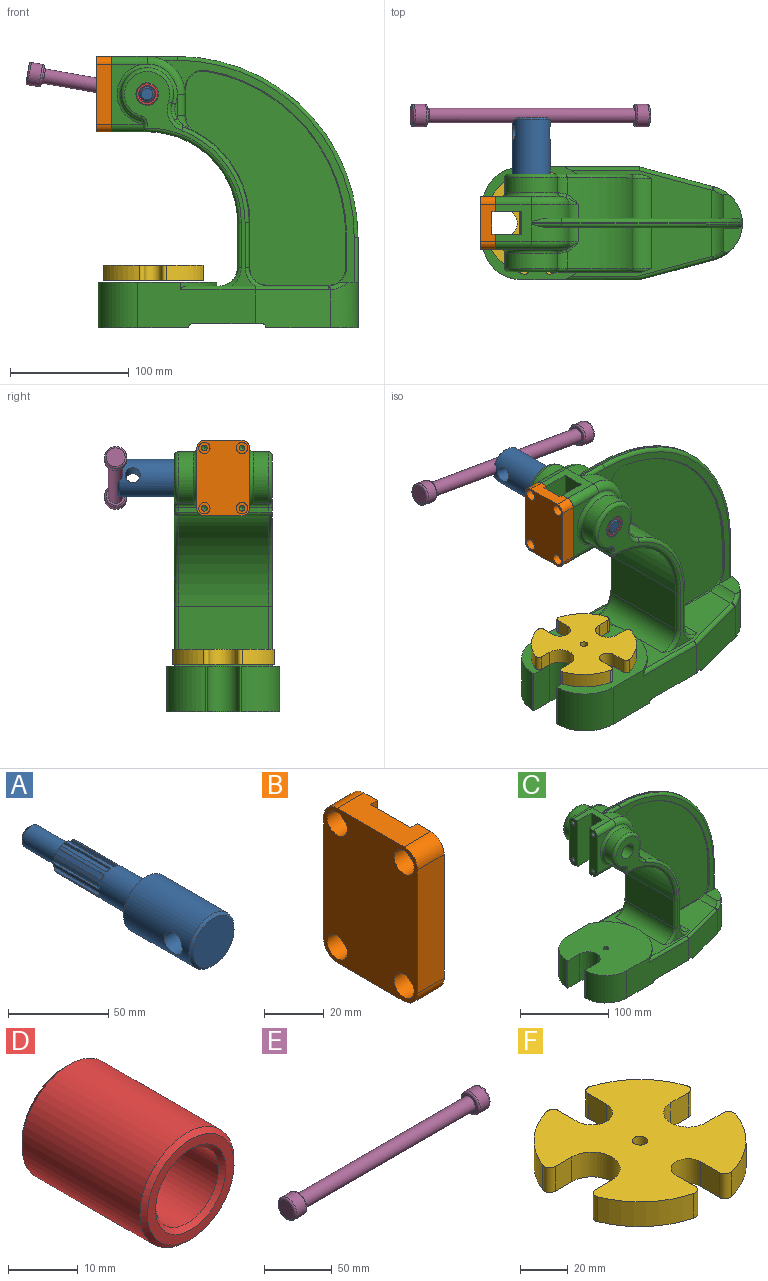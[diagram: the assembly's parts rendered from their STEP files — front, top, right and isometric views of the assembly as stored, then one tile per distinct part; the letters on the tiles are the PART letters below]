
ASSEMBLY  parts=6 mates=4
PART A: 94 faces, bbox 31.8x130.2x31.8 mm
  f0: cone r=8mm half-angle=45deg, axis (0,-1,0), area 3.4mm2, adj f11,f18,f83,f87
  f1: cone r=8mm half-angle=45deg, axis (0,-1,0), area 3.4mm2, adj f11,f18,f77,f81
  f2: cone r=8mm half-angle=45deg, axis (0,-1,0), area 3.4mm2, adj f11,f18,f71,f75
  f3: cone r=8mm half-angle=45deg, axis (0,-1,0), area 3.4mm2, adj f11,f18,f65,f69
  f4: cone r=8mm half-angle=45deg, axis (0,-1,0), area 3.4mm2, adj f11,f18,f59,f63
  f5: cone r=8mm half-angle=45deg, axis (0,-1,0), area 3.4mm2, adj f11,f18,f53,f57
  f6: cone r=8mm half-angle=45deg, axis (0,-1,0), area 3.4mm2, adj f11,f18,f47,f51
  f7: cone r=8mm half-angle=45deg, axis (0,-1,0), area 3.4mm2, adj f11,f18,f41,f45
  f8: cone r=8mm half-angle=45deg, axis (0,-1,0), area 3.4mm2, adj f11,f18,f35,f39
  f9: cone r=8mm half-angle=45deg, axis (0,-1,0), area 3.4mm2, adj f11,f18,f29,f33
  f10: cone r=8mm half-angle=45deg, axis (0,-1,0), area 3.4mm2, adj f11,f18,f23,f27
  f11: cylinder r=9.53mm len=55.63mm, axis (0,-1,0), area 2118.8mm2, adj f0,f1,f2,f3,f4,f5,f6,f7
  f12: plane 31.75x31.75mm, normal (0,1,0), area 506.7mm2, adj f11,f13
  f13: cylinder r=15.88mm len=46.1mm, axis (0,-1,0), area 4339.6mm2, adj f12,f15,f16
  f14: plane 28.7x28.7mm, normal (0,-1,0), area 647mm2, adj f15
  f15: cone r=14.35mm half-angle=45deg, axis (0,1,0), area 204.7mm2, adj f13,f14
  f16: cylinder r=6.35mm len=31.75mm, axis (1,0,0), area 1214.5mm2, adj f13
  f17: cylinder r=6.35mm len=23.88mm, axis (0,1,0), area 952.6mm2, adj f18,f93
  f18: plane 16x16mm, normal (0,1,0), area 67.3mm2, adj f0,f1,f2,f3,f4,f5,f6,f7
  f19: plane 9.65x9.65mm, normal (0,1,0), area 73.2mm2, adj f93
  f20: cone r=8mm half-angle=45deg, axis (0,-1,0), area 3.4mm2, adj f11,f18,f21,f89
  f21: plane 31.76x1.55mm, normal (0.36,0,-0.93), area 51.4mm2, adj f11,f18,f20,f22,f24
  f22: plane 31.75x2.7mm, normal (0.97,0,0.26), area 88.7mm2, adj f18,f21,f23,f25
  f23: plane 31.76x1.65mm, normal (-0.15,0,0.99), area 51.4mm2, adj f10,f11,f18,f22,f26
  f24: cone r=1.78mm half-angle=83.9deg, axis (0.26,0,-0.97), area 1.5mm2, adj f11,f21,f25
  f25: cylinder r=1.78mm len=3.16mm, axis (0.26,0,-0.97), area 7.7mm2, adj f11,f22,f24,f26
  f26: cone r=0mm half-angle=83.9deg, axis (-0.26,0,0.97), area 1.5mm2, adj f11,f23,f25
  f27: plane 31.76x1.65mm, normal (-0.15,0,-0.99), area 51.4mm2, adj f10,f11,f18,f28,f30
  f28: plane 31.75x2.7mm, normal (0.97,0,-0.26), area 88.7mm2, adj f18,f27,f29,f31
  f29: plane 31.76x1.55mm, normal (0.36,0,0.93), area 51.4mm2, adj f9,f11,f18,f28,f32
  f30: cone r=1.78mm half-angle=83.9deg, axis (-0.26,0,-0.97), area 1.5mm2, adj f11,f27,f31
  f31: cylinder r=1.78mm len=3.16mm, axis (-0.26,0,-0.97), area 7.7mm2, adj f11,f28,f30,f32
  f32: cone r=0mm half-angle=83.9deg, axis (0.26,0,0.97), area 1.5mm2, adj f11,f29,f31
  f33: plane 31.76x1.3mm, normal (-0.63,0,-0.78), area 51.4mm2, adj f9,f11,f18,f34,f36
  f34: plane 31.75x1.98mm, normal (0.71,0,-0.71), area 88.7mm2, adj f18,f33,f35,f37
  f35: plane 31.76x1.3mm, normal (0.78,0,0.63), area 51.4mm2, adj f8,f11,f18,f34,f38
  f36: cone r=1.78mm half-angle=83.9deg, axis (-0.71,0,-0.71), area 1.5mm2, adj f11,f33,f37
  f37: cylinder r=1.78mm len=3.16mm, axis (-0.71,0,-0.71), area 7.5mm2, adj f11,f34,f36,f38
  f38: cone r=0mm half-angle=83.9deg, axis (0.71,0,0.71), area 1.5mm2, adj f11,f35,f37
  f39: plane 31.76x1.55mm, normal (-0.93,0,-0.36), area 51.4mm2, adj f8,f11,f18,f40,f42
  f40: plane 31.75x2.7mm, normal (0.26,0,-0.97), area 88.7mm2, adj f18,f39,f41,f43
  f41: plane 31.76x1.65mm, normal (0.99,0,0.15), area 51.4mm2, adj f7,f11,f18,f40,f44
  f42: cone r=1.78mm half-angle=83.9deg, axis (-0.97,0,-0.26), area 1.5mm2, adj f11,f39,f43
  f43: cylinder r=1.78mm len=3.16mm, axis (-0.97,0,-0.26), area 7.7mm2, adj f11,f40,f42,f44
  f44: cone r=0mm half-angle=83.9deg, axis (0.97,0,0.26), area 1.5mm2, adj f11,f41,f43
  f45: plane 31.76x1.65mm, normal (-0.99,0,0.15), area 51.4mm2, adj f7,f11,f18,f46,f48
  f46: plane 31.75x2.7mm, normal (-0.26,0,-0.97), area 88.7mm2, adj f18,f45,f47,f49
  f47: plane 31.76x1.55mm, normal (0.93,0,-0.36), area 51.4mm2, adj f6,f11,f18,f46,f50
  f48: cone r=1.78mm half-angle=83.9deg, axis (-0.97,0,0.26), area 1.5mm2, adj f11,f45,f49
  f49: cylinder r=1.78mm len=3.16mm, axis (-0.97,0,0.26), area 7.7mm2, adj f11,f46,f48,f50
  f50: cone r=0mm half-angle=83.9deg, axis (0.97,0,-0.26), area 1.5mm2, adj f11,f47,f49
  f51: plane 31.76x1.3mm, normal (-0.78,0,0.63), area 51.4mm2, adj f6,f11,f18,f52,f54
  f52: plane 31.75x1.98mm, normal (-0.71,0,-0.71), area 88.7mm2, adj f18,f51,f53,f55
  f53: plane 31.76x1.3mm, normal (0.63,0,-0.78), area 51.4mm2, adj f5,f11,f18,f52,f56
  f54: cone r=1.78mm half-angle=83.9deg, axis (-0.71,0,0.71), area 1.5mm2, adj f11,f51,f55
  f55: cylinder r=1.78mm len=3.16mm, axis (-0.71,0,0.71), area 7.5mm2, adj f11,f52,f54,f56
  f56: cone r=0mm half-angle=83.9deg, axis (0.71,0,-0.71), area 1.5mm2, adj f11,f53,f55
  f57: plane 31.76x1.55mm, normal (-0.36,0,0.93), area 51.4mm2, adj f5,f11,f18,f58,f60
  f58: plane 31.75x2.7mm, normal (-0.97,0,-0.26), area 88.7mm2, adj f18,f57,f59,f61
  f59: plane 31.76x1.65mm, normal (0.15,0,-0.99), area 51.4mm2, adj f4,f11,f18,f58,f62
  f60: cone r=1.78mm half-angle=83.9deg, axis (-0.26,0,0.97), area 1.5mm2, adj f11,f57,f61
  f61: cylinder r=1.78mm len=3.16mm, axis (-0.26,0,0.97), area 7.7mm2, adj f11,f58,f60,f62
  f62: cone r=0mm half-angle=83.9deg, axis (0.26,0,-0.97), area 1.5mm2, adj f11,f59,f61
  f63: plane 31.76x1.65mm, normal (0.15,0,0.99), area 51.4mm2, adj f4,f11,f18,f64,f66
  f64: plane 31.75x2.7mm, normal (-0.97,0,0.26), area 88.7mm2, adj f18,f63,f65,f67
  f65: plane 31.76x1.55mm, normal (-0.36,0,-0.93), area 51.4mm2, adj f3,f11,f18,f64,f68
  f66: cone r=1.78mm half-angle=83.9deg, axis (0.26,0,0.97), area 1.5mm2, adj f11,f63,f67
  f67: cylinder r=1.78mm len=3.16mm, axis (0.26,0,0.97), area 7.7mm2, adj f11,f64,f66,f68
  f68: cone r=0mm half-angle=83.9deg, axis (-0.26,0,-0.97), area 1.5mm2, adj f11,f65,f67
  f69: plane 31.76x1.3mm, normal (0.63,0,0.78), area 51.4mm2, adj f3,f11,f18,f70,f72
  f70: plane 31.75x1.98mm, normal (-0.71,0,0.71), area 88.7mm2, adj f18,f69,f71,f73
  f71: plane 31.76x1.3mm, normal (-0.78,0,-0.63), area 51.4mm2, adj f2,f11,f18,f70,f74
  f72: cone r=1.78mm half-angle=83.9deg, axis (0.71,0,0.71), area 1.5mm2, adj f11,f69,f73
  f73: cylinder r=1.78mm len=3.16mm, axis (0.71,0,0.71), area 7.5mm2, adj f11,f70,f72,f74
  f74: cone r=0mm half-angle=83.9deg, axis (-0.71,0,-0.71), area 1.5mm2, adj f11,f71,f73
  f75: plane 31.76x1.55mm, normal (0.93,0,0.36), area 51.4mm2, adj f2,f11,f18,f76,f78
  f76: plane 31.75x2.7mm, normal (-0.26,0,0.97), area 88.7mm2, adj f18,f75,f77,f79
  f77: plane 31.76x1.65mm, normal (-0.99,0,-0.15), area 51.4mm2, adj f1,f11,f18,f76,f80
  f78: cone r=1.78mm half-angle=83.9deg, axis (0.97,0,0.26), area 1.5mm2, adj f11,f75,f79
  f79: cylinder r=1.78mm len=3.16mm, axis (0.97,0,0.26), area 7.7mm2, adj f11,f76,f78,f80
  f80: cone r=0mm half-angle=83.9deg, axis (-0.97,0,-0.26), area 1.5mm2, adj f11,f77,f79
  f81: plane 31.76x1.65mm, normal (0.99,0,-0.15), area 51.4mm2, adj f1,f11,f18,f82,f84
  f82: plane 31.75x2.7mm, normal (0.26,0,0.97), area 88.7mm2, adj f18,f81,f83,f85
  f83: plane 31.76x1.55mm, normal (-0.93,0,0.36), area 51.4mm2, adj f0,f11,f18,f82,f86
  f84: cone r=1.78mm half-angle=83.9deg, axis (0.97,0,-0.26), area 1.5mm2, adj f11,f81,f85
  f85: cylinder r=1.78mm len=3.16mm, axis (0.97,0,-0.26), area 7.7mm2, adj f11,f82,f84,f86
  f86: cone r=0mm half-angle=83.9deg, axis (-0.97,0,0.26), area 1.5mm2, adj f11,f83,f85
  f87: plane 31.76x1.3mm, normal (0.78,0,-0.63), area 51.4mm2, adj f0,f11,f18,f88,f90
  f88: plane 31.75x1.98mm, normal (0.71,0,0.71), area 88.7mm2, adj f18,f87,f89,f91
  f89: plane 31.76x1.3mm, normal (-0.63,0,0.78), area 51.4mm2, adj f11,f18,f20,f88,f92
  f90: cone r=1.78mm half-angle=83.9deg, axis (0.71,0,-0.71), area 1.5mm2, adj f11,f87,f91
  f91: cylinder r=1.78mm len=3.16mm, axis (0.71,0,-0.71), area 7.5mm2, adj f11,f88,f90,f92
  f92: cone r=0mm half-angle=83.9deg, axis (-0.71,0,0.71), area 1.5mm2, adj f11,f89,f91
  f93: cone r=4.83mm half-angle=45deg, axis (0,-1,0), area 75.7mm2, adj f17,f19
PART B: 26 faces, bbox 12.7x44.5x63.5 mm
  f0: plane 63.5x12.7mm, normal (1,0,0), area 753.5mm2, adj f1,f2,f6,f7,f8,f14,f17,f25
  f1: cylinder r=6.35mm len=12.7mm, axis (1,0,0), area 126.7mm2, adj f0,f2,f8,f9
  f2: plane 31.75x12.7mm, normal (0,0,1), area 341.8mm2, adj f0,f1,f3,f9,f10,f23,f24,f25
  f3: cylinder r=6.35mm len=12.7mm, axis (1,0,0), area 126.7mm2, adj f2,f4,f9,f10
  f4: plane 50.8x12.7mm, normal (0,1,0), area 645.2mm2, adj f3,f5,f9,f10
  f5: cylinder r=6.35mm len=12.7mm, axis (1,0,0), area 126.7mm2, adj f4,f6,f9,f10
  f6: plane 31.75x12.7mm, normal (0,0,-1), area 341.8mm2, adj f0,f5,f7,f9,f10,f23,f24,f25
  f7: cylinder r=6.35mm len=12.7mm, axis (1,0,0), area 126.7mm2, adj f0,f6,f8,f9
  f8: plane 50.8x12.7mm, normal (0,-1,0), area 645.2mm2, adj f0,f1,f7,f9
  f9: plane 63.5x44.45mm, normal (-1,0,0), area 2502.9mm2, adj f1,f2,f3,f4,f5,f6,f7,f8
  f10: plane 63.5x12.7mm, normal (1,0,0), area 753.5mm2, adj f2,f3,f4,f5,f6,f11,f20,f24
  f11: cylinder r=2.38mm len=6.35mm, axis (-1,0,0), area 95mm2, adj f10,f12
  f12: plane 9.53x9.53mm, normal (-1,0,0), area 53.4mm2, adj f11,f13
  f13: cylinder r=4.76mm len=9.53mm, axis (-1,0,0), area 190mm2, adj f9,f12
  f14: cylinder r=2.38mm len=6.35mm, axis (-1,0,0), area 95mm2, adj f0,f15
  f15: plane 9.53x9.53mm, normal (-1,0,0), area 53.4mm2, adj f14,f16
  f16: cylinder r=4.76mm len=9.53mm, axis (-1,0,0), area 190mm2, adj f9,f15
  f17: cylinder r=2.38mm len=6.35mm, axis (-1,0,0), area 95mm2, adj f0,f18
  f18: plane 9.53x9.53mm, normal (-1,0,0), area 53.4mm2, adj f17,f19
  f19: cylinder r=4.76mm len=9.53mm, axis (-1,0,0), area 190mm2, adj f9,f18
  f20: cylinder r=2.38mm len=6.35mm, axis (-1,0,0), area 95mm2, adj f10,f21
  f21: plane 9.53x9.53mm, normal (-1,0,0), area 53.4mm2, adj f20,f22
  f22: cylinder r=4.76mm len=9.53mm, axis (-1,0,0), area 190mm2, adj f9,f21
  f23: plane 63.5x19.05mm, normal (1,0,0), area 1209.7mm2, adj f2,f6,f24,f25
  f24: plane 63.5x3.23mm, normal (0,-1,0), area 204.8mm2, adj f2,f6,f10,f23
  f25: plane 63.5x3.23mm, normal (0,1,0), area 204.8mm2, adj f0,f2,f6,f23
PART C: 180 faces, bbox 234.5x98.1x244 mm
  f0: plane 63.5x12.7mm, normal (-1,0,0), area 753.5mm2, adj f2,f15,f17,f92,f97,f149,f151,f158
  f1: plane 20.23x2.34mm, normal (0,1,0), area 23.9mm2, adj f90,f91,f104,f106
  f2: plane 50.8x30.1mm, normal (0,-1,0), area 515.4mm2, adj f0,f83,f92,f97,f124
  f3: plane 22.59x12.73mm, normal (1,0,0), area 235.4mm2, adj f19,f26,f32,f87,f94,f174
  f4: plane 22.59x12.73mm, normal (1,0,0), area 235.4mm2, adj f10,f14,f33,f86,f90,f164
  f5: plane 99.19x38.1mm, normal (0,-1,0), area 3202mm2, adj f6,f40,f46,f49,f52,f58,f76,f133
  f6: plane 100x95.25mm, normal (0,0,1), area 7398mm2, adj f5,f43,f44,f48,f54,f55,f56,f57
  f7: plane 38.1x34.96mm, normal (1,0,0), area 1331.9mm2, adj f8,f9,f114,f169
  f8: cylinder r=15.88mm len=34.96mm, axis (0,1,0), area 871.7mm2, adj f7,f37,f115,f167
  f9: cylinder r=85.72mm len=80.21mm, axis (0,1,0), area 3442.3mm2, adj f7,f80,f86,f100,f113,f168
  f10: cylinder r=15.88mm len=18.65mm, axis (0,1,0), area 22.7mm2, adj f4,f11,f33,f162
  f11: cylinder r=142.88mm len=140.67mm, axis (0,1,0), area 163.3mm2, adj f10,f12,f33,f160
  f12: plane 25.4x0.82mm, normal (-1,0,0), area 20.8mm2, adj f11,f13,f33,f161
  f13: cylinder r=15.88mm len=24.81mm, axis (0,1,0), area 242.1mm2, adj f12,f33,f37,f45,f139,f140,f163
  f14: cylinder r=31.75mm len=31.75mm, axis (0,1,0), area 616.8mm2, adj f4,f15,f33,f89,f141
  f15: plane 55.5x31.75mm, normal (0,0,1), area 573.2mm2, adj f0,f14,f16,f19,f31,f88,f92,f141
  f16: plane 63.5x12.7mm, normal (-1,0,0), area 753.5mm2, adj f15,f17,f21,f88,f96,f147,f153,f157
  f17: plane 31.75x30.1mm, normal (0,0,-1), area 533.2mm2, adj f0,f16,f18,f96,f97,f156,f157,f158
  f18: cylinder r=76.2mm len=76.2mm, axis (0,1,0), area 9120.7mm2, adj f17,f22,f103,f105,f119,f121
  f19: cylinder r=31.75mm len=31.75mm, axis (0,1,0), area 616.8mm2, adj f3,f15,f32,f93,f144
  f20: plane 20.23x2.34mm, normal (0,-1,0), area 23.9mm2, adj f94,f95,f122,f124
  f21: plane 50.8x30.1mm, normal (0,1,0), area 515.4mm2, adj f16,f78,f88,f96,f106
  f22: plane 76.2x38.1mm, normal (-1,0,0), area 2903.2mm2, adj f18,f98,f101,f117
  f23: cylinder r=15.88mm len=34.96mm, axis (0,1,0), area 871.7mm2, adj f24,f37,f132,f177
  f24: plane 38.1x34.96mm, normal (1,0,0), area 1331.9mm2, adj f23,f25,f131,f179
  f25: cylinder r=85.72mm len=80.21mm, axis (0,1,0), area 3442.3mm2, adj f24,f81,f87,f118,f130,f178
  f26: cylinder r=15.88mm len=18.65mm, axis (0,1,0), area 22.7mm2, adj f3,f27,f32,f172
  f27: cylinder r=142.88mm len=140.67mm, axis (0,1,0), area 163.3mm2, adj f26,f28,f32,f170
  f28: plane 25.4x0.82mm, normal (-1,0,0), area 20.8mm2, adj f27,f29,f32,f171
  f29: cylinder r=15.88mm len=24.81mm, axis (0,1,0), area 242.1mm2, adj f28,f32,f36,f37,f135,f136,f173
  f30: plane 76.2x7.92mm, normal (1,0,0), area 361.9mm2, adj f31,f36,f42,f45,f51,f53,f143,f146
  f31: cylinder r=152.4mm len=152.4mm, axis (0,1,0), area 377mm2, adj f15,f30,f142,f145
  f32: plane 187.33x160.79mm, normal (0,-1,0), area 1900.4mm2, adj f3,f19,f26,f27,f28,f29,f36,f144
  f33: plane 187.33x160.79mm, normal (0,1,0), area 1900.4mm2, adj f4,f10,f11,f12,f13,f14,f45,f141
  f34: plane 180.67x135mm, normal (0,-1,0), area 14138.8mm2, adj f170,f171,f172,f173,f174,f175,f176,f177
  f35: plane 180.67x135mm, normal (0,1,0), area 14138.8mm2, adj f160,f161,f162,f163,f164,f165,f166,f167
  f36: plane 26.58x18.73mm, normal (0,0,1), area 245.8mm2, adj f29,f30,f32,f53,f136,f146
  f37: plane 119.12x89.67mm, normal (0,0,1), area 4280.2mm2, adj f8,f13,f23,f29,f76,f77,f84,f98
  f38: cylinder r=3.17mm len=9.06mm, axis (0,1,0), area 40.9mm2, adj f40,f42,f52,f69
  f39: cylinder r=3.17mm len=7.93mm, axis (0,1,0), area 39.5mm2, adj f41,f46,f48,f65
  f40: plane 58.73x9.7mm, normal (0,0,-1), area 467.1mm2, adj f5,f38,f49,f52,f64,f69
  f41: plane 58.73x9.7mm, normal (0,0,-1), area 467.1mm2, adj f39,f47,f48,f50,f65,f67
  f42: plane 90.55x77.8mm, normal (0,0,-1), area 1454mm2, adj f30,f38,f47,f50,f51,f52,f53,f59
  f43: plane 38.1x1.61mm, normal (-1,0,0), area 61.5mm2, adj f6,f46,f54,f58
  f44: plane 38.1x1.61mm, normal (-1,0,0), area 61.5mm2, adj f6,f46,f55,f57
  f45: plane 26.58x18.73mm, normal (0,0,1), area 245.8mm2, adj f13,f30,f33,f51,f140,f143
  f46: plane 95.25x76.2mm, normal (0,0,-1), area 2029.8mm2, adj f5,f39,f43,f44,f48,f49,f54,f55
  f47: cylinder r=3.17mm len=9.06mm, axis (0,1,0), area 40.9mm2, adj f41,f42,f50,f67
  f48: plane 99.19x38.1mm, normal (0,1,0), area 3202mm2, adj f6,f39,f41,f46,f50,f57,f76,f137
  f49: cylinder r=3.17mm len=7.93mm, axis (0,1,0), area 39.5mm2, adj f5,f40,f46,f64
  f50: plane 63.64x32.15mm, normal (0.26,0.97,0), area 2053.6mm2, adj f41,f42,f47,f48,f51,f138,f139
  f51: cylinder r=31.75mm len=38.1mm, axis (0,0,-1), area 1379.2mm2, adj f30,f42,f45,f50,f140
  f52: plane 63.64x32.15mm, normal (0.26,-0.97,0), area 2053.6mm2, adj f5,f38,f40,f42,f53,f134,f135
  f53: cylinder r=31.75mm len=38.1mm, axis (0,0,-1), area 1379.2mm2, adj f30,f36,f42,f52,f136
  f54: plane 38.1x19.05mm, normal (0,1,0), area 725.8mm2, adj f6,f43,f46,f56
  f55: plane 38.1x19.05mm, normal (0,-1,0), area 725.8mm2, adj f6,f44,f46,f56
  f56: cylinder r=13.49mm len=38.1mm, axis (0,0,-1), area 1615.1mm2, adj f6,f46,f54,f55
  f57: cylinder r=33.32mm len=38.1mm, axis (0,0,-1), area 1963.7mm2, adj f6,f44,f46,f48
  f58: cylinder r=33.32mm len=38.1mm, axis (0,0,-1), area 1963.7mm2, adj f5,f6,f43,f46
  f59: plane 30.18x6.86mm, normal (-1,0,0), area 207mm2, adj f42,f60,f68,f70
  f60: plane 31.27x5.6mm, normal (0,0,-1), area 124.1mm2, adj f59,f61,f68,f70
  f61: cylinder r=23.8mm len=46.06mm, axis (0,1,0), area 499.2mm2, adj f60,f62,f67,f68,f69,f70
  f62: plane 84.13x79.4mm, normal (0,0,-1), area 5642.5mm2, adj f61,f64,f65,f66,f67,f69
  f63: plane 100.62x79.4mm, normal (0,0,-1), area 6568.5mm2, adj f64,f65,f66,f71,f72,f73,f74,f75
  f64: plane 98.15x30.18mm, normal (0,1,0), area 2718.8mm2, adj f40,f46,f49,f62,f63,f66,f69,f75
  f65: plane 98.15x30.18mm, normal (0,-1,0), area 2718.8mm2, adj f39,f41,f46,f62,f63,f66,f67,f74
  f66: plane 79.4x3.18mm, normal (-1,0,0), area 252.1mm2, adj f62,f63,f64,f65
  f67: plane 62.63x27.36mm, normal (-0.26,-0.97,0), area 1710.8mm2, adj f41,f42,f47,f61,f62,f65,f68
  f68: cylinder r=23.83mm len=30.18mm, axis (0,0,-1), area 814.8mm2, adj f42,f59,f60,f61,f67
  f69: plane 62.63x27.36mm, normal (-0.26,0.97,0), area 1710.8mm2, adj f38,f40,f42,f61,f62,f64,f70
  f70: cylinder r=23.83mm len=30.18mm, axis (0,0,-1), area 814.8mm2, adj f42,f59,f60,f61,f69
  f71: plane 30.18x10.12mm, normal (0,-1,0), area 305.3mm2, adj f46,f63,f73,f75
  f72: plane 30.18x10.12mm, normal (0,1,0), area 305.3mm2, adj f46,f63,f73,f74
  f73: cylinder r=21.42mm len=42.84mm, axis (0,0,-1), area 2030.4mm2, adj f46,f63,f71,f72
  f74: cylinder r=25.4mm len=30.18mm, axis (0,0,-1), area 986.2mm2, adj f46,f63,f65,f72
  f75: cylinder r=25.4mm len=30.18mm, axis (0,0,-1), area 986.2mm2, adj f46,f63,f64,f71
  f76: cylinder r=52.37mm len=95.25mm, axis (0,0,1), area 401mm2, adj f5,f6,f37,f48,f133,f137
  f77: plane 180.98x110.12mm, normal (0,1,0), area 1717.8mm2, adj f37,f85,f99,f101,f103,f109,f110,f111
  f78: plane 16.73x3.98mm, normal (-1,0,0), area 64.1mm2, adj f21,f96,f105,f106,f108,f109
  f79: cylinder r=22.23mm len=44.45mm, axis (0,1,0), area 1356.2mm2, adj f80,f106,f108,f111
  f80: cylinder r=15.88mm len=20.22mm, axis (0,1,0), area 319.4mm2, adj f9,f79,f102,f104,f112
  f81: cylinder r=15.88mm len=20.22mm, axis (0,1,0), area 319.4mm2, adj f25,f82,f120,f122,f129
  f82: cylinder r=22.23mm len=44.45mm, axis (0,1,0), area 1356.2mm2, adj f81,f124,f126,f128
  f83: plane 16.73x3.98mm, normal (-1,0,0), area 64.1mm2, adj f2,f97,f121,f124,f125,f126
  f84: plane 180.98x110.12mm, normal (0,-1,0), area 1717.8mm2, adj f37,f85,f116,f117,f119,f125,f127,f128
  f85: cylinder r=9.53mm len=82.55mm, axis (0,1,0), area 4727mm2, adj f77,f84,f156,f157,f158,f159
  f86: cylinder r=15.88mm len=14.02mm, axis (0,1,0), area 218.9mm2, adj f4,f9,f91,f166
  f87: cylinder r=15.88mm len=14.02mm, axis (0,1,0), area 218.9mm2, adj f3,f25,f95,f176
  f88: cylinder r=6.35mm len=30.1mm, axis (-1,0,0), area 300.2mm2, adj f15,f16,f21,f89
  f89: torus R=25.4mm, axis (0,-1,0), area 461.3mm2, adj f14,f88,f90,f106
  f90: cylinder r=6.35mm len=18.2mm, axis (0,0,1), area 181.6mm2, adj f1,f4,f89,f91
  f91: torus R=22.23mm, axis (0,-1,0), area 98mm2, adj f1,f86,f90,f100,f102
  f92: cylinder r=6.35mm len=30.1mm, axis (1,0,0), area 300.2mm2, adj f0,f2,f15,f93
  f93: torus R=25.4mm, axis (0,-1,0), area 461.3mm2, adj f19,f92,f94,f124
  f94: cylinder r=6.35mm len=18.2mm, axis (0,0,-1), area 181.6mm2, adj f3,f20,f93,f95
  f95: torus R=22.23mm, axis (0,-1,0), area 98mm2, adj f20,f87,f94,f118,f120
  f96: cylinder r=6.35mm len=30.1mm, axis (1,0,0), area 279.1mm2, adj f16,f17,f21,f78,f105
  f97: cylinder r=6.35mm len=30.1mm, axis (-1,0,0), area 279.1mm2, adj f0,f2,f17,f83,f121
  f98: cylinder r=15.88mm len=76.2mm, axis (0,-1,0), area 1900.2mm2, adj f22,f37,f99,f116
  f99: torus R=19.05mm, axis (0,-1,0), area 107.7mm2, adj f37,f77,f98,f101
  f100: bspline ~12.01x8.85mm, area 17.9mm2, adj f9,f91,f102
  f101: cylinder r=3.17mm len=38.1mm, axis (0,0,-1), area 190mm2, adj f22,f77,f99,f103
  f102: bspline ~10.6x9.56mm, area 36.6mm2, adj f80,f91,f100,f104
  f103: torus R=79.38mm, axis (0,-1,0), area 606mm2, adj f18,f77,f101,f107
  f104: torus R=12.7mm, axis (0,-1,0), area 70.6mm2, adj f1,f80,f102,f106
  f105: cylinder r=3.17mm len=22.23mm, axis (0,1,0), area 97.1mm2, adj f18,f78,f96,f107
  f106: torus R=25.4mm, axis (0,-1,0), area 570mm2, adj f1,f21,f78,f79,f89,f104,f108
  f107: sphere r=3.17mm, area 21.6mm2, adj f103,f105,f109
  f108: cylinder r=3.17mm len=15.82mm, axis (0,1,0), area 59.7mm2, adj f78,f79,f106,f110
  f109: cylinder r=3.17mm len=3.98mm, axis (0,0,-1), area 19.9mm2, adj f77,f78,f107,f110
  f110: torus R=6.35mm, axis (0,-1,0), area 28.5mm2, adj f77,f108,f109,f111
  f111: torus R=19.05mm, axis (0,-1,0), area 504.9mm2, adj f77,f79,f110,f112
  f112: torus R=19.05mm, axis (0,-1,0), area 132.1mm2, adj f77,f80,f111,f113
  f113: torus R=82.55mm, axis (0,-1,0), area 510.4mm2, adj f9,f77,f112,f114
  f114: cylinder r=3.17mm len=38.1mm, axis (0,0,1), area 190mm2, adj f7,f77,f113,f115
  f115: torus R=19.05mm, axis (0,-1,0), area 107.7mm2, adj f8,f37,f77,f114
  f116: torus R=19.05mm, axis (0,-1,0), area 107.7mm2, adj f37,f84,f98,f117
  f117: cylinder r=3.17mm len=38.1mm, axis (0,0,1), area 190mm2, adj f22,f84,f116,f119
  f118: bspline ~11.06x8.44mm, area 17.9mm2, adj f25,f95,f120
  f119: torus R=79.38mm, axis (0,-1,0), area 606mm2, adj f18,f84,f117,f123
  f120: bspline ~9.12x8.99mm, area 36.6mm2, adj f81,f95,f118,f122
  f121: cylinder r=3.17mm len=22.23mm, axis (0,1,0), area 97.1mm2, adj f18,f83,f97,f123
  f122: torus R=12.7mm, axis (0,-1,0), area 70.6mm2, adj f20,f81,f120,f124
  f123: sphere r=3.17mm, area 15.8mm2, adj f119,f121,f125
  f124: torus R=25.4mm, axis (0,-1,0), area 570mm2, adj f2,f20,f82,f83,f93,f122,f126
  f125: cylinder r=3.17mm len=3.98mm, axis (0,0,1), area 19.9mm2, adj f83,f84,f123,f127
  f126: cylinder r=3.17mm len=15.82mm, axis (0,1,0), area 59.7mm2, adj f82,f83,f124,f127
  f127: torus R=6.35mm, axis (0,-1,0), area 28.5mm2, adj f84,f125,f126,f128
  f128: torus R=19.05mm, axis (0,-1,0), area 504.9mm2, adj f82,f84,f127,f129
  f129: torus R=19.05mm, axis (0,-1,0), area 132.1mm2, adj f81,f84,f128,f130
  f130: torus R=82.55mm, axis (0,-1,0), area 510.4mm2, adj f25,f84,f129,f131
  f131: cylinder r=3.17mm len=38.1mm, axis (0,0,-1), area 190mm2, adj f24,f84,f130,f132
  f132: torus R=19.05mm, axis (0,-1,0), area 107.7mm2, adj f23,f37,f84,f131
  f133: cylinder r=3.17mm len=63.09mm, axis (1,0,0), area 298.9mm2, adj f5,f37,f76,f134
  f134: cylinder r=3.17mm len=62.81mm, axis (0.97,0.26,0), area 319mm2, adj f37,f52,f133,f135
  f135: bspline ~3.41x3.21mm, area 6mm2, adj f29,f52,f134,f136
  f136: bspline ~18.95x11.92mm, area 79.7mm2, adj f29,f36,f53,f135
  f137: cylinder r=3.17mm len=63.09mm, axis (-1,0,0), area 298.9mm2, adj f37,f48,f76,f138
  f138: cylinder r=3.17mm len=62.81mm, axis (-0.97,0.26,0), area 319mm2, adj f37,f50,f137,f139
  f139: bspline ~6.89x4.84mm, area 6mm2, adj f13,f50,f138,f140
  f140: bspline ~17.46x11.57mm, area 79.7mm2, adj f13,f45,f51,f139
  f141: cylinder r=3.17mm len=25.4mm, axis (-1,0,0), area 92.2mm2, adj f14,f15,f33,f142
  f142: torus R=149.22mm, axis (0,-1,0), area 1184.9mm2, adj f31,f33,f141,f143
  f143: cylinder r=3.17mm len=38.1mm, axis (0,0,1), area 190mm2, adj f30,f33,f45,f142
  f144: cylinder r=3.17mm len=25.4mm, axis (1,0,0), area 92.2mm2, adj f15,f19,f32,f145
  f145: torus R=149.22mm, axis (0,-1,0), area 1184.9mm2, adj f31,f32,f144,f146
  f146: cylinder r=3.17mm len=38.1mm, axis (0,0,-1), area 190mm2, adj f30,f32,f36,f145
  f147: cylinder r=2.38mm len=6.35mm, axis (-1,0,0), area 95mm2, adj f16,f148
  f148: cone r=0mm half-angle=59deg, axis (-1,0,0), area 20.8mm2, adj f147
  f149: cylinder r=2.38mm len=6.35mm, axis (-1,0,0), area 95mm2, adj f0,f150
  f150: cone r=0mm half-angle=59deg, axis (-1,0,0), area 20.8mm2, adj f149
  f151: cylinder r=2.38mm len=6.35mm, axis (-1,0,0), area 95mm2, adj f0,f152
  f152: cone r=0mm half-angle=59deg, axis (-1,0,0), area 20.8mm2, adj f151
  f153: cylinder r=2.38mm len=6.35mm, axis (-1,0,0), area 95mm2, adj f16,f154
  f154: cone r=0mm half-angle=59deg, axis (-1,0,0), area 20.8mm2, adj f153
  f155: cylinder r=3.17mm len=7.93mm, axis (0,0,1), area 158.1mm2, adj f6,f63
  f156: plane 26.47x19.05mm, normal (-1,0,0), area 504.2mm2, adj f17,f85,f157,f158
  f157: plane 63.5x22.17mm, normal (0,-1,0), area 1396.6mm2, adj f15,f16,f17,f85,f156,f159
  f158: plane 63.5x22.17mm, normal (0,1,0), area 1396.6mm2, adj f0,f15,f17,f85,f156,f159
  f159: plane 26.47x19.05mm, normal (-1,0,0), area 504.2mm2, adj f15,f85,f157,f158
  f160: torus R=142.11mm, axis (0,-1,0), area 238.1mm2, adj f11,f35,f161,f162
  f161: cylinder r=0.76mm len=25.4mm, axis (0,0,1), area 30.4mm2, adj f12,f35,f160,f163
  f162: torus R=15.11mm, axis (0,-1,0), area 32.6mm2, adj f10,f35,f160,f164
  f163: torus R=15.11mm, axis (0,-1,0), area 29.3mm2, adj f13,f35,f161,f165
  f164: cylinder r=0.76mm len=22.59mm, axis (0,0,1), area 27mm2, adj f4,f35,f162,f166
  f165: cylinder r=0.76mm len=50.8mm, axis (1,0,0), area 60.8mm2, adj f35,f37,f163,f167
  f166: torus R=15.11mm, axis (0,-1,0), area 20.2mm2, adj f35,f86,f164,f168
  f167: torus R=15.11mm, axis (0,-1,0), area 29.3mm2, adj f8,f35,f165,f169
  f168: torus R=86.49mm, axis (0,-1,0), area 111.5mm2, adj f9,f35,f166,f169
  f169: cylinder r=0.76mm len=38.1mm, axis (0,0,-1), area 45.6mm2, adj f7,f35,f167,f168
  f170: torus R=142.11mm, axis (0,-1,0), area 238.1mm2, adj f27,f34,f171,f172
  f171: cylinder r=0.76mm len=25.4mm, axis (0,0,-1), area 30.4mm2, adj f28,f34,f170,f173
  f172: torus R=15.11mm, axis (0,-1,0), area 32.6mm2, adj f26,f34,f170,f174
  f173: torus R=15.11mm, axis (0,-1,0), area 29.3mm2, adj f29,f34,f171,f175
  f174: cylinder r=0.76mm len=22.59mm, axis (0,0,-1), area 27mm2, adj f3,f34,f172,f176
  f175: cylinder r=0.76mm len=50.8mm, axis (-1,0,0), area 60.8mm2, adj f34,f37,f173,f177
  f176: torus R=15.11mm, axis (0,-1,0), area 20.2mm2, adj f34,f87,f174,f178
  f177: torus R=15.11mm, axis (0,-1,0), area 29.3mm2, adj f23,f34,f175,f179
  f178: torus R=86.49mm, axis (0,-1,0), area 111.5mm2, adj f25,f34,f176,f179
  f179: cylinder r=0.76mm len=38.1mm, axis (0,0,1), area 45.6mm2, adj f24,f34,f177,f178
PART D: 8 faces, bbox 19.1x25.4x19.1 mm
  f0: plane 17.53x17.53mm, normal (0,-1,0), area 82.3mm2, adj f4,f5
  f1: plane 17.53x17.53mm, normal (0,1,0), area 82.3mm2, adj f6,f7
  f2: cylinder r=9.53mm len=23.88mm, axis (0,1,0), area 1428.9mm2, adj f4,f7
  f3: cylinder r=6.35mm len=23.88mm, axis (0,1,0), area 952.6mm2, adj f5,f6
  f4: cone r=9.53mm half-angle=45deg, axis (0,1,0), area 61.9mm2, adj f0,f2
  f5: cone r=6.35mm half-angle=45deg, axis (0,-1,0), area 45.6mm2, adj f0,f3
  f6: cone r=6.35mm half-angle=45deg, axis (0,1,0), area 45.6mm2, adj f1,f3
  f7: cone r=9.53mm half-angle=45deg, axis (0,-1,0), area 61.9mm2, adj f1,f2
PART E: 12 faces, bbox 203.2x20.6x20.6 mm
  f0: cylinder r=6.1mm len=176.28mm, axis (-1,0,0), area 6751.8mm2, adj f5,f7
  f1: cylinder r=9.53mm len=19.05mm, axis (-1,0,0), area 577.6mm2, adj f10,f11
  f2: plane 16x16mm, normal (1,0,0), area 18.7mm2, adj f7,f11
  f3: plane 16x16mm, normal (-1,0,0), area 201.1mm2, adj f10
  f4: cylinder r=9.53mm len=19.05mm, axis (1,0,0), area 577.6mm2, adj f8,f9
  f5: plane 16x16mm, normal (-1,0,0), area 84.4mm2, adj f0,f9
  f6: plane 16x16mm, normal (1,0,0), area 201.1mm2, adj f8
  f7: torus R=7.62mm, axis (-1,0,0), area 100mm2, adj f0,f2
  f8: torus R=8mm, axis (1,0,0), area 134.9mm2, adj f4,f6
  f9: torus R=8mm, axis (1,0,0), area 134.9mm2, adj f4,f5
  f10: torus R=8mm, axis (1,0,0), area 134.9mm2, adj f1,f3
  f11: torus R=8mm, axis (-1,0,0), area 134.9mm2, adj f1,f2
PART F: 27 faces, bbox 83.8x85.8x12.7 mm
  f0: cylinder r=44.45mm len=28.56mm, axis (0,0,-1), area 510.6mm2, adj f17,f18,f19,f25
  f1: plane 12.7x9.85mm, normal (0,-1,0), area 125.1mm2, adj f2,f17,f18,f25
  f2: cylinder r=11.9mm len=23.8mm, axis (0,0,-1), area 474.8mm2, adj f1,f3,f17,f18
  f3: plane 12.7x9.85mm, normal (0,1,0), area 125.1mm2, adj f2,f17,f18,f26
  f4: cylinder r=44.45mm len=30.27mm, axis (0,0,-1), area 533.1mm2, adj f17,f18,f20,f26
  f5: plane 12.7x11.39mm, normal (1,0,0), area 144.7mm2, adj f6,f17,f18,f20
  f6: cylinder r=7.14mm len=14.28mm, axis (0,0,-1), area 284.8mm2, adj f5,f7,f17,f18
  f7: plane 12.7x11.39mm, normal (-1,0,0), area 144.7mm2, adj f6,f17,f18,f21
  f8: cylinder r=44.45mm len=30.9mm, axis (0,0,-1), area 556.3mm2, adj f17,f18,f21,f22
  f9: plane 12.7x10.43mm, normal (0,1,0), area 132.5mm2, adj f10,f17,f18,f22
  f10: cylinder r=10.31mm len=20.62mm, axis (0,0,-1), area 411.4mm2, adj f9,f11,f17,f18
  f11: plane 12.7x10.43mm, normal (0,-1,0), area 132.5mm2, adj f10,f17,f18,f23
  f12: cylinder r=44.45mm len=29.19mm, axis (0,0,-1), area 533.7mm2, adj f17,f18,f23,f24
  f13: plane 12.7x10.95mm, normal (-1,0,0), area 139mm2, adj f14,f17,f18,f24
  f14: cylinder r=8.72mm len=17.45mm, axis (0,0,-1), area 348.1mm2, adj f13,f15,f17,f18
  f15: plane 12.7x10.95mm, normal (1,0,0), area 139mm2, adj f14,f17,f18,f19
  f16: cylinder r=3.17mm len=12.7mm, axis (0,0,-1), area 253.4mm2, adj f17,f18
  f17: plane 85.84x83.78mm, normal (0,0,1), area 4373.8mm2, adj f0,f1,f2,f3,f4,f5,f6,f7
  f18: plane 85.84x83.78mm, normal (0,0,-1), area 4373.8mm2, adj f0,f1,f2,f3,f4,f5,f6,f7
  f19: cylinder r=3.17mm len=12.7mm, axis (0,0,-1), area 75.1mm2, adj f0,f15,f17,f18
  f20: cylinder r=3.17mm len=12.7mm, axis (0,0,-1), area 73.5mm2, adj f4,f5,f17,f18
  f21: cylinder r=3.17mm len=12.7mm, axis (0,0,-1), area 73.5mm2, adj f7,f8,f17,f18
  f22: cylinder r=3.17mm len=12.7mm, axis (0,0,-1), area 76.8mm2, adj f8,f9,f17,f18
  f23: cylinder r=3.17mm len=12.7mm, axis (0,0,-1), area 76.8mm2, adj f11,f12,f17,f18
  f24: cylinder r=3.17mm len=12.7mm, axis (0,0,-1), area 75.1mm2, adj f12,f13,f17,f18
  f25: cylinder r=3.17mm len=12.7mm, axis (0,0,-1), area 78.4mm2, adj f0,f1,f17,f18
  f26: cylinder r=3.17mm len=12.7mm, axis (0,0,-1), area 78.4mm2, adj f3,f4,f17,f18
PLACE A rot(axis=(-0.09,0,-1),180deg) t=(-99.86,-32.53,61.12)mm
PLACE B t=(-99.86,-32.53,61.12)mm
PLACE C t=(-99.86,-32.53,61.12)mm fixed
PLACE D t=(-99.86,-89.68,61.12)mm
PLACE E rot(axis=(0.99,0.06,-0.09),112.1deg) t=(-88.46,29.91,130.96)mm
PLACE F t=(-101.21,-32.36,62.77)mm
MATE fastened B.f11 <-> C.f147  axis (1,0,0) through (-129.96,-16.66,86.52)mm
MATE pin_slot E.f0 <-> A.f16  axis (-0.99,0,0.17) through (-99.86,58.18,61.12)mm
MATE fastened C.f9 <-> C.f14  axis (0,-1,0) through (-99.86,-73.81,-46.83)mm
MATE revolute C.f14 <-> A.f0  axis (0,-1,0) through (-99.86,-73.81,61.12)mm
